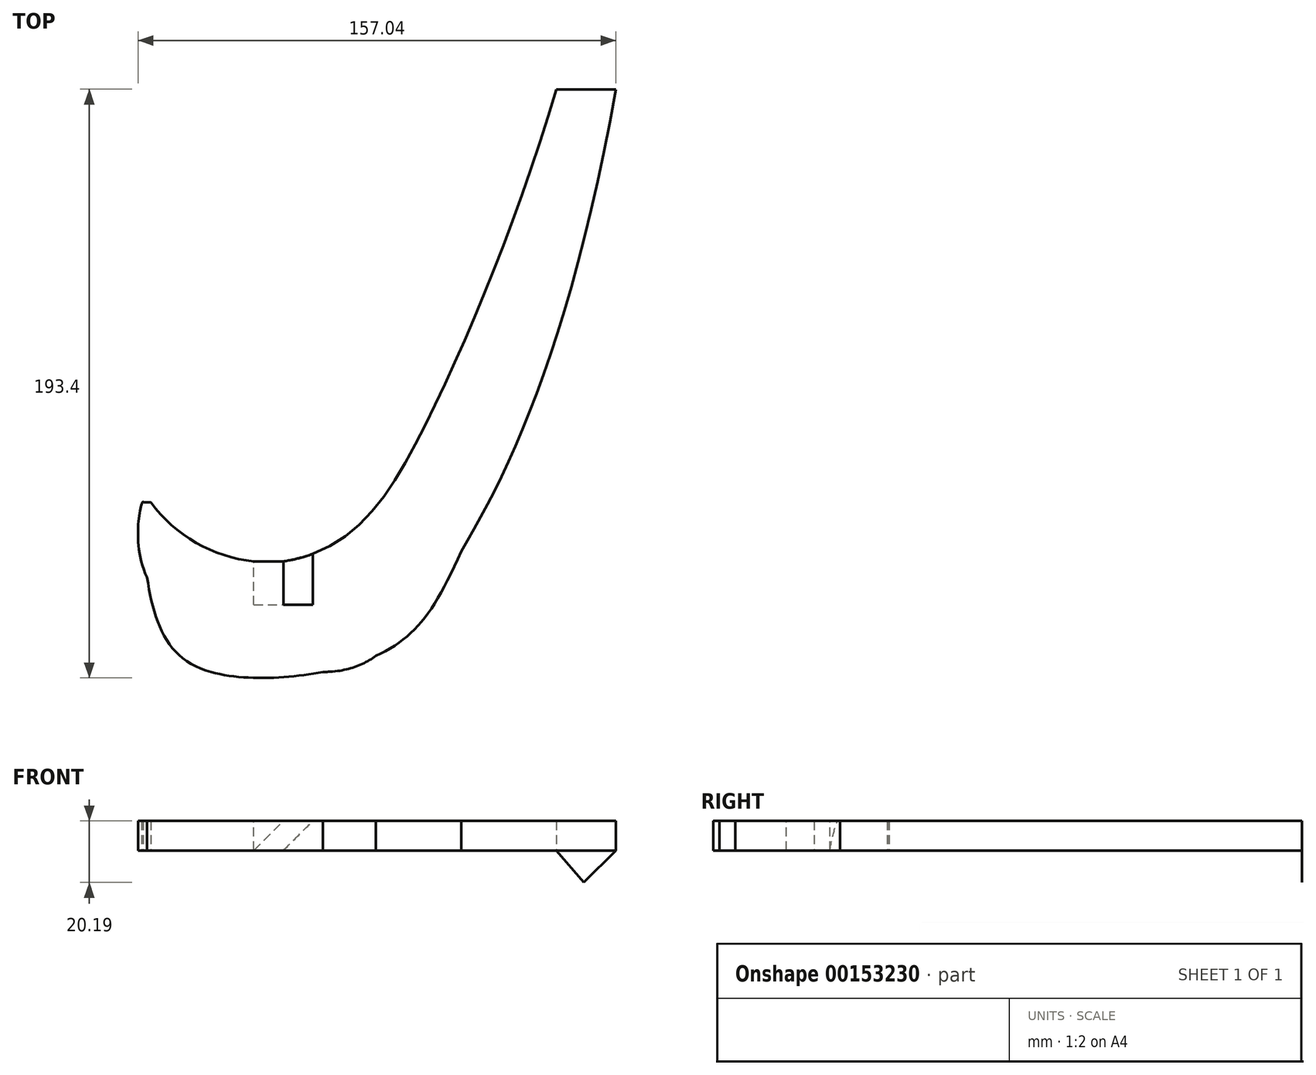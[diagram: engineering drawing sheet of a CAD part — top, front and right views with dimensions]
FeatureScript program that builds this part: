
annotation { "Feature Type Name" : "Feature", "Feature Type Description" : "" }
export const myFeature = defineFeature(function(context is Context, id is Id, definition is map)
    precondition{}
    {
        {
            var Q0;
            Q0=qCreatedBy(makeId("Top.planeOp"),FACE);
            var sketch = newSketch(context, id + "F0", { "sketchPlane" : qUnion([Q0])});
            skArc(sketch, "E0", {"start": v(-38.73, -28.25) * mm, "mid": v(-23.8, -41.61) * mm, "end": v(-4.72, -47.7) * mm});
            skLineSegment(sketch, "E1", {"start": v(94.58, 107.4) * mm, "end": v(114.12, 107.4) * mm});
            skFitSpline(sketch, "E2", {"points": [v(-38.73, -28.25) * mm, v(-40.94, -28.25) * mm, v(-41.43, -28.25) * mm, v(-39.97, -52.74) * mm, v(-26, -81.05) * mm, v(17.24, -84.12) * mm, v(44.51, -73.13) * mm, v(63.45, -44) * mm, v(114.12, 107.4) * mm], "startDerivative": vector(-142.13, -5.85) * mm, "endDerivative": vector(144.55, 567.75) * mm});
            skFitSpline(sketch, "E3", {"points": [v(-34.91, -28.25) * mm, v(-41.03, -28.33) * mm, v(-41.32, -28.16) * mm, v(-40, -52.82) * mm, v(17.24, -84) * mm, v(42.04, -72.93) * mm, v(63.5, -44.03) * mm, v(114.8, 111.27) * mm], "startDerivative": vector(-142.13, -5.85) * mm, "endDerivative": vector(137.87, 796.34) * mm});
            skLineSegment(sketch, "E4", {"start": v(-18.9, -84.02) * mm, "end": v(20.24, -83.95) * mm});
            skLineSegment(sketch, "E5", {"start": v(0, 0) * mm, "end": v(0, -52.86) * mm, "construction": true});
            skLineSegment(sketch, "E6.bottom", {"start": v(-4.84, -62) * mm, "end": v(4.84, -62) * mm});
            skLineSegment(sketch, "E6.left", {"start": v(-4.84, -62) * mm, "end": v(-4.84, -47.7) * mm});
            skLineSegment(sketch, "E6.right", {"start": v(4.84, -62) * mm, "end": v(4.84, -47.7) * mm});
            skPoint(sketch, "E6.middle", {"position": v(0, -52.86) * mm});
            skFitSpline(sketch, "E7", {"points": [v(94.58, 107.4) * mm, v(50.83, -4.15) * mm, v(4.84, -47.7) * mm], "startDerivative": vector(-65.8, -218.5) * mm, "endDerivative": vector(-170.03, -26.08) * mm});
            skSolve(sketch);
        }
        {
            var Q0;
            Q0 = qSketchRegion(id + "F0", true);
            extrude(context, id + "F1", {"entities" : qUnion([Q0]), "depth" : 9.68 * mm});
        }
        {
            var Q0;
            Q0=makeQuery(id+"F1.opExtrude","SWEPT_FACE",FACE,{"disambiguationData":[OSD([sQuery(id+"F0.wireOp",EDGE,"E1")])]});
            var sketch = newSketch(context, id + "F2", { "sketchPlane" : qUnion([Q0])});
            skLineSegment(sketch, "E8", {"start": v(-114.12, 0) * mm, "end": v(-103.61, -10.5) * mm});
            skLineSegment(sketch, "E9", {"start": v(-94.58, 0) * mm, "end": v(-103.61, -10.5) * mm});
            skSolve(sketch);
        }
        {
            var Q0;
            Q0=makeQuery(id+"F2.imprint","IMPRINT",FACE,{"disambiguationData":[TD([[makeQuery(id+"F2.imprint","IMPRINT",EDGE,{"derivedFrom":sQuery(id+"F2.wireOp",EDGE,"E8")}),1.0]])]});
            extrude(context, id + "F3", {"entities" : qUnion([Q0]), "depth" : 0 * mm});
        }
        {
            var Q0;
            Q0=makeQuery(id+"F1.opExtrude","SWEPT_FACE",FACE,{"disambiguationData":[OSD([sQuery(id+"F0.wireOp",EDGE,"E6.bottom")])]});
            var sketch = newSketch(context, id + "F4", { "sketchPlane" : qUnion([Q0])});
            skLineSegment(sketch, "E10", {"start": v(0, 9.68) * mm, "end": v(0, 0) * mm, "construction": true});
            skLineSegment(sketch, "E11", {"start": v(-4.84, 0) * mm, "end": v(-14.52, 9.68) * mm});
            skLineSegment(sketch, "E12", {"start": v(-14.52, 9.68) * mm, "end": v(-4.84, 9.68) * mm});
            skLineSegment(sketch, "E13", {"start": v(4.84, 0) * mm, "end": v(-4.84, 9.68) * mm});
            skLineSegment(sketch, "E14", {"start": v(4.84, 9.68) * mm, "end": v(-4.84, 9.68) * mm});
            skLineSegment(sketch, "E15", {"start": v(4.84, 9.68) * mm, "end": v(4.84, 0) * mm});
            skLineSegment(sketch, "E16", {"start": v(-4.84, 0) * mm, "end": v(-4.84, 9.68) * mm});
            skSolve(sketch);
        }
        {
            var Q0;
            Q0=makeQuery(id+"F4.imprint","IMPRINT",FACE,{"disambiguationData":[TD([[makeQuery(id+"F4.imprint","IMPRINT",EDGE,{"derivedFrom":sQuery(id+"F4.wireOp",EDGE,"E11")}),-1.0]])]});
            extrude(context, id + "F5", {"entities" : qUnion([Q0]), "operationType" : NewBodyOperationType.REMOVE, "depth" : 17.01 * mm});
        }
        {
            var Q0;
            Q0=makeQuery(id+"F4.imprint","IMPRINT",FACE,{"disambiguationData":[TD([[makeQuery(id+"F4.imprint","IMPRINT",EDGE,{"derivedFrom":sQuery(id+"F4.wireOp",EDGE,"E13")}),-1.0]])]});
            extrude(context, id + "F6", {"entities" : qUnion([Q0]), "operationType" : NewBodyOperationType.ADD, "depth" : 14.3 * mm});
        }
    });
